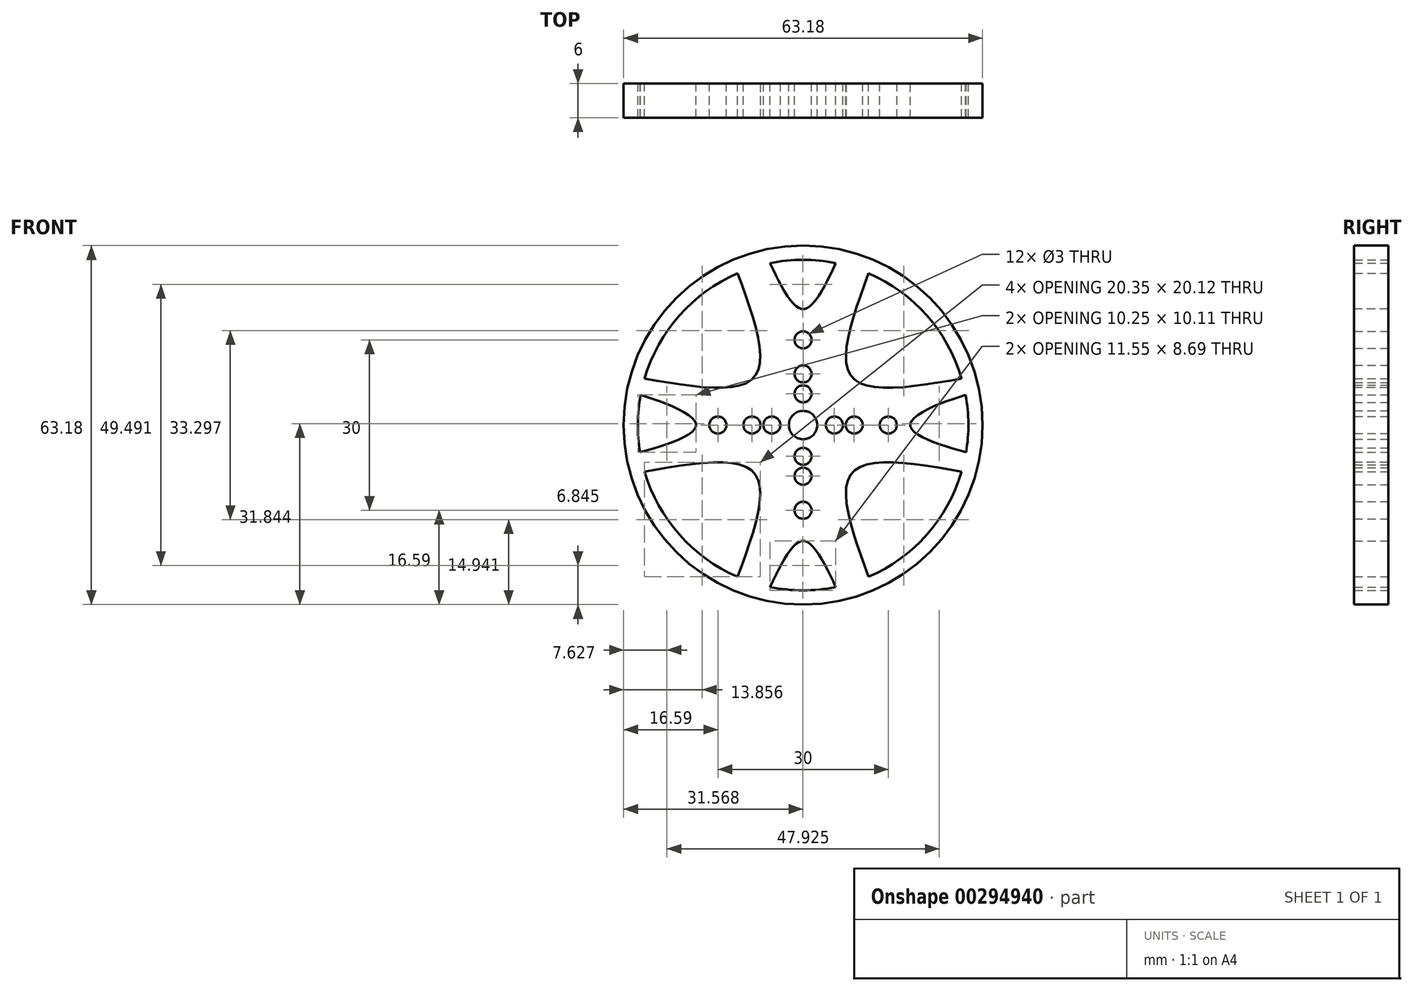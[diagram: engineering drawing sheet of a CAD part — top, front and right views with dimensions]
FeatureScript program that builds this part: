
annotation { "Feature Type Name" : "Feature", "Feature Type Description" : "" }
export const myFeature = defineFeature(function(context is Context, id is Id, definition is map)
    precondition{}
    {
        {
            var Q0;
            Q0=qCreatedBy(makeId("Front.planeOp"),FACE);
            var sketch = newSketch(context, id + "F0", { "sketchPlane" : qUnion([Q0])});
            skCircle(sketch, "E0", {"center": v(0, 0) * mm, "radius": 31.59 * mm});
            skCircle(sketch, "E1", {"center": v(0, 0) * mm, "radius": 2.5 * mm});
            skCircle(sketch, "E2", {"center": v(0, 9) * mm, "radius": 1.5 * mm});
            skCircle(sketch, "E3", {"center": v(0, 15) * mm, "radius": 1.5 * mm});
            skCircle(sketch, "E4", {"center": v(9, 0) * mm, "radius": 1.5 * mm});
            skCircle(sketch, "E5", {"center": v(15, 0) * mm, "radius": 1.5 * mm});
            skCircle(sketch, "E6", {"center": v(0, 5.5) * mm, "radius": 1.5 * mm});
            skCircle(sketch, "E7", {"center": v(5.5, 0) * mm, "radius": 1.5 * mm});
            skCircle(sketch, "E8.MirrorC", {"center": v(0, -5.5) * mm, "radius": 1.5 * mm});
            skCircle(sketch, "E9.MirrorC", {"center": v(0, -9) * mm, "radius": 1.5 * mm});
            skCircle(sketch, "E10.MirrorC", {"center": v(0, -15) * mm, "radius": 1.5 * mm});
            skCircle(sketch, "E11.MirrorC", {"center": v(-5.5, 0) * mm, "radius": 1.5 * mm});
            skCircle(sketch, "E12.MirrorC", {"center": v(-9, 0) * mm, "radius": 1.5 * mm});
            skCircle(sketch, "E13.MirrorC", {"center": v(-15, 0) * mm, "radius": 1.5 * mm});
            skArc(sketch, "E14", {"start": v(-28.6, 5.3) * mm, "mid": v(-29.09, 0.26) * mm, "end": v(-28.7, -4.8) * mm});
            skFitSpline(sketch, "E15", {"points": [v(28.6, 5.3) * mm, v(18.84, 0) * mm, v(28.7, -4.8) * mm], "startDerivative": vector(-24.84, -7.75) * mm, "endDerivative": vector(25.55, -6.94) * mm});
            skFitSpline(sketch, "E16", {"points": [v(-5.8, -28.5) * mm, v(0, -20.4) * mm, v(5.75, -28.52) * mm], "startDerivative": vector(11.6, 24.25) * mm, "endDerivative": vector(11.49, -24.28) * mm});
            skFitSpline(sketch, "E17", {"points": [v(11.53, -26.7) * mm, v(8.59, -8.46) * mm, v(27.91, -8.2) * mm], "startDerivative": vector(-16.84, 45.85) * mm, "endDerivative": vector(49.33, -8.66) * mm});
            skFitSpline(sketch, "E18.MirrorCS", {"points": [v(-28.6, 5.3) * mm, v(-18.84, 0) * mm, v(-28.7, -4.8) * mm], "startDerivative": vector(24.84, -7.75) * mm, "endDerivative": vector(-25.55, -6.94) * mm});
            skFitSpline(sketch, "E19.MirrorCS", {"points": [v(-11.53, -26.7) * mm, v(-8.59, -8.46) * mm, v(-27.91, -8.2) * mm], "startDerivative": vector(16.84, 45.85) * mm, "endDerivative": vector(-49.33, -8.66) * mm});
            skFitSpline(sketch, "E20.MirrorCS", {"points": [v(-5.8, 28.5) * mm, v(0, 20.4) * mm, v(5.75, 28.52) * mm], "startDerivative": vector(11.6, -24.25) * mm, "endDerivative": vector(11.49, 24.28) * mm});
            skFitSpline(sketch, "E21.MirrorCS", {"points": [v(11.53, 26.7) * mm, v(8.59, 8.46) * mm, v(27.91, 8.2) * mm], "startDerivative": vector(-16.84, -45.85) * mm, "endDerivative": vector(49.33, 8.66) * mm});
            skFitSpline(sketch, "E22.MirrorCS", {"points": [v(-11.53, 26.7) * mm, v(-8.59, 8.46) * mm, v(-27.91, 8.2) * mm], "startDerivative": vector(16.84, -45.85) * mm, "endDerivative": vector(-49.33, 8.66) * mm});
            skArc(sketch, "E23.trimOffspring", {"start": v(-27.91, -8.2) * mm, "mid": v(-21.78, -19.28) * mm, "end": v(-11.53, -26.7) * mm});
            skArc(sketch, "E24.trimOffspring", {"start": v(-5.8, -28.5) * mm, "mid": v(-0.02, -29.09) * mm, "end": v(5.75, -28.52) * mm});
            skArc(sketch, "E25.trimOffspring", {"start": v(11.53, -26.7) * mm, "mid": v(21.78, -19.28) * mm, "end": v(27.91, -8.2) * mm});
            skArc(sketch, "E26.trimOffspring", {"start": v(28.7, -4.8) * mm, "mid": v(29.09, 0.26) * mm, "end": v(28.6, 5.3) * mm});
            skArc(sketch, "E27.trimOffspring", {"start": v(27.91, 8.2) * mm, "mid": v(21.78, 19.28) * mm, "end": v(11.53, 26.7) * mm});
            skArc(sketch, "E28.trimOffspring", {"start": v(5.75, 28.52) * mm, "mid": v(-0.02, 29.09) * mm, "end": v(-5.8, 28.5) * mm});
            skArc(sketch, "E29.trimOffspring", {"start": v(-11.53, 26.7) * mm, "mid": v(-21.78, 19.28) * mm, "end": v(-27.91, 8.2) * mm});
            skSolve(sketch);
        }
        {
            var Q0;
            Q0=makeQuery(id+"F0.imprint","IMPRINT",FACE,{"disambiguationData":[TD([[makeQuery(id+"F0.imprint","IMPRINT",EDGE,{"derivedFrom":sQuery(id+"F0.wireOp",EDGE,"E0")}),1.0]])]});
            extrude(context, id + "F1", {"entities" : qUnion([Q0]), "depth" : 6 * mm});
        }
    });
